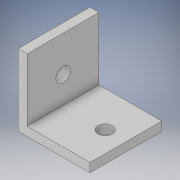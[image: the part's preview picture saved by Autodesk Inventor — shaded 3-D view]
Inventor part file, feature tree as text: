
AUTODESK INVENTOR PART (.ipt)
format: ipt  version: 2018 (Build 220112000, 112)  size: 113,664 bytes
history: native  units: in
note: dims shown in document units (in); Inventor stores cm internally (conversion verified against a paired STEP export)
features: extrude x3, sketch x3
ambient origin geometry x8: Origin, YZ Plane, XZ Plane, XY Plane, X Axis, Y Axis, Z Axis, Center Point
bodies: Solid1 (feature_tree)
feature tree (6):
  extrude  "Extrusion1"  Depth=1.0in
  extrude  "Extrusion2"  Depth=0.125in
  extrude  "Extrusion3"  Depth=1.0in
  sketch  "Sketch1"  dims[d0=0.125in d1=1.0in]
  sketch  "Sketch2"  dims[d2=1.0in d3=0.125in]
  sketch  "Sketch3"  dims[d4=1.0in d5=0.0in d6=0.5in d7=0.2031in d8=1.0in d9=0.0in d10=0.712in d11=0.2031in d12=1.0in d13=0.0in]
